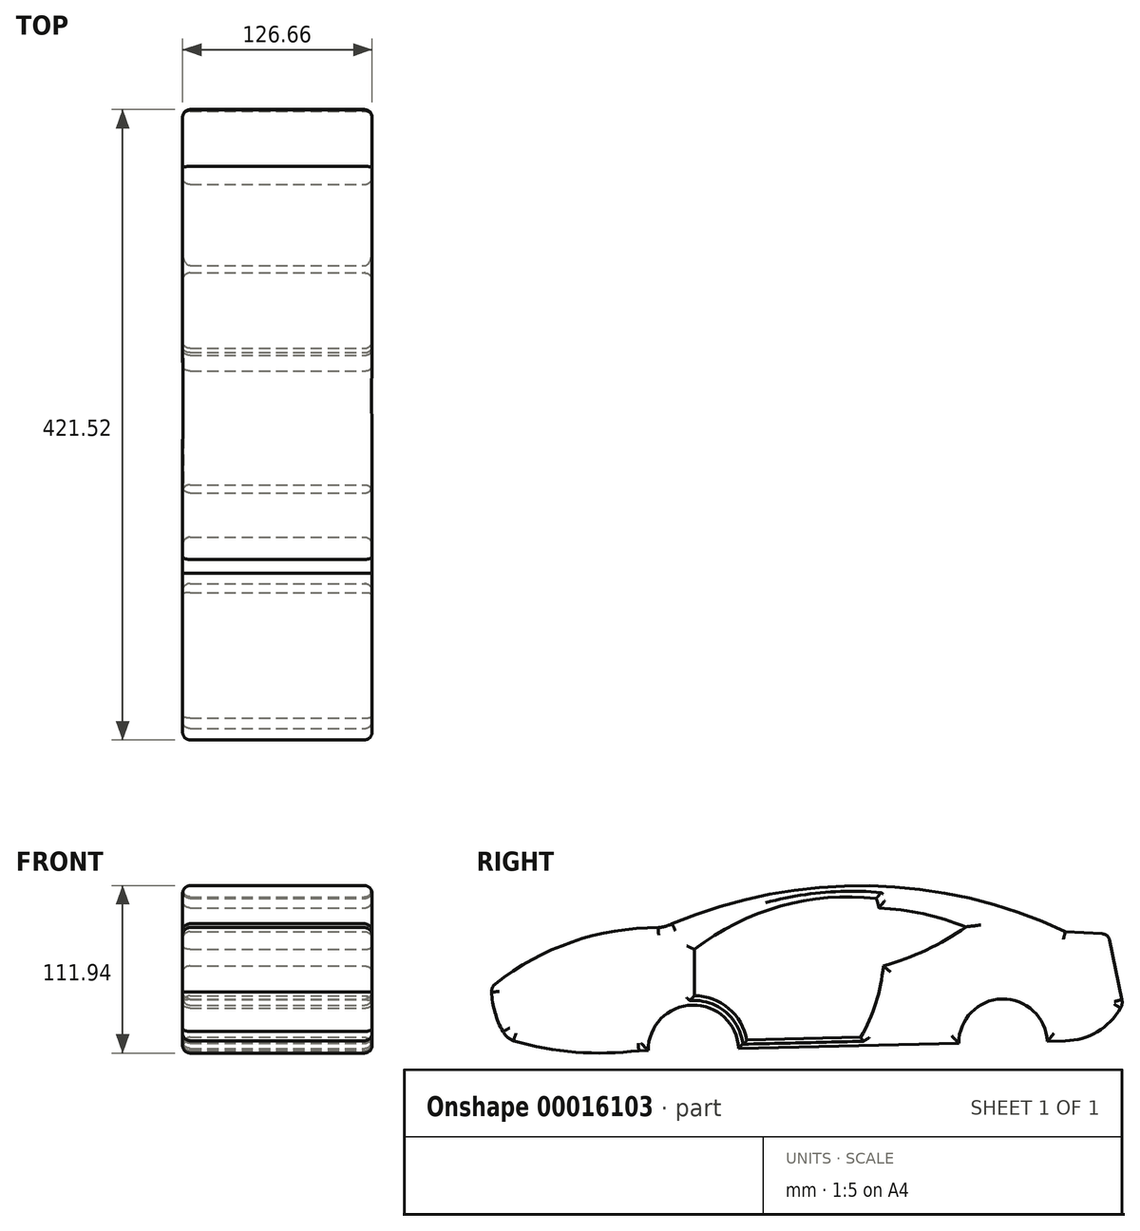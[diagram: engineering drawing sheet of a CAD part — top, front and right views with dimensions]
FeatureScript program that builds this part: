
annotation { "Feature Type Name" : "Feature", "Feature Type Description" : "" }
export const myFeature = defineFeature(function(context is Context, id is Id, definition is map)
    precondition{}
    {
        {
            var Q0;
            Q0=qCreatedBy(makeId("Right.planeOp"),FACE);
            var sketch = newSketch(context, id + "F0", { "sketchPlane" : qUnion([Q0])});
            skArc(sketch, "E0", {"start": v(-83.48, 39.7) * mm, "mid": v(-78.75, 40.5) * mm, "end": v(-74.28, 42.24) * mm});
            skArc(sketch, "E1", {"start": v(188.64, 37) * mm, "mid": v(57.74, 67.65) * mm, "end": v(-74.28, 42.24) * mm});
            skArc(sketch, "E2", {"start": v(-83.48, 39.7) * mm, "mid": v(-141.17, 30.08) * mm, "end": v(-192.5, 2.04) * mm});
            skArc(sketch, "E3", {"start": v(140.42, 60.51) * mm, "mid": v(137.05, 59.2) * mm, "end": v(134.3, 56.86) * mm});
            skArc(sketch, "E4", {"start": v(140.42, 60.51) * mm, "mid": v(129.16, 62.69) * mm, "end": v(117.85, 60.78) * mm});
            skLineSegment(sketch, "E5", {"start": v(188.64, 37) * mm, "end": v(217.28, 35.28) * mm});
            skArc(sketch, "E6", {"start": v(225.5, -14.08) * mm, "mid": v(226.53, -11.4) * mm, "end": v(226.34, -8.53) * mm});
            skLineSegment(sketch, "E7", {"start": v(226.34, -8.53) * mm, "end": v(217.28, 35.28) * mm});
            skArc(sketch, "E8", {"start": v(188.64, -36.07) * mm, "mid": v(209.97, -29.93) * mm, "end": v(225.5, -14.08) * mm});
            skArc(sketch, "E9", {"start": v(-29.85, -41.03) * mm, "mid": v(-60.8, -12.14) * mm, "end": v(-90.3, -42.51) * mm});
            skLineSegment(sketch, "E10", {"start": v(-90.3, -42.51) * mm, "end": v(-96.57, -42.66) * mm});
            skArc(sketch, "E11", {"start": v(176.48, -36.35) * mm, "mid": v(146.27, -8.07) * mm, "end": v(117.37, -37.69) * mm});
            skLineSegment(sketch, "E12", {"start": v(176.48, -36.35) * mm, "end": v(188.64, -36.07) * mm});
            skLineSegment(sketch, "E13", {"start": v(117.37, -37.69) * mm, "end": v(-29.85, -41.03) * mm});
            skPoint(sketch, "E14", {"position": v(-78.75, 40.5) * mm});
            skPoint(sketch, "E15.visualSharp", {"position": v(-195.03, 0) * mm});
            skArc(sketch, "E15.filletArc", {"start": v(-192.5, 2.04) * mm, "mid": v(-194.36, -0.36) * mm, "end": v(-194.9, -3.36) * mm});
            skArc(sketch, "E16", {"start": v(-187.3, -29.8) * mm, "mid": v(-184.44, -33.58) * mm, "end": v(-180.37, -36) * mm});
            skPoint(sketch, "E17", {"position": v(-180.37, -36) * mm});
            skPoint(sketch, "E18", {"position": v(-187.3, -29.8) * mm});
            skArc(sketch, "E19", {"start": v(-180.37, -36) * mm, "mid": v(-138.8, -43.56) * mm, "end": v(-96.57, -42.66) * mm});
            skArc(sketch, "E20", {"start": v(-194.9, -3.36) * mm, "mid": v(-192.72, -17.05) * mm, "end": v(-187.3, -29.8) * mm});
            skLineSegment(sketch, "E21", {"start": v(-59.36, 25.5) * mm, "end": v(-59.36, -5.92) * mm});
            skArc(sketch, "E22", {"start": v(-24.3, -35.53) * mm, "mid": v(-36.46, -14.36) * mm, "end": v(-59.36, -5.92) * mm});
            skArc(sketch, "E23", {"start": v(62.24, 59.21) * mm, "mid": v(-1.9, 54.03) * mm, "end": v(-59.36, 25.05) * mm});
            skArc(sketch, "E24", {"start": v(122.1, 40.18) * mm, "mid": v(93.57, 48.87) * mm, "end": v(64, 52.88) * mm});
            skArc(sketch, "E25", {"start": v(55.2, 53.43) * mm, "mid": v(-0.36, 46.83) * mm, "end": v(-51.63, 24.43) * mm});
            skArc(sketch, "E26", {"start": v(-51.71, 24.4) * mm, "mid": v(2.04, 10.5) * mm, "end": v(57.48, 13.55) * mm});
            skArc(sketch, "E27", {"start": v(66.94, 14.01) * mm, "mid": v(95.68, 24.66) * mm, "end": v(122.1, 40.18) * mm});
            skArc(sketch, "E28", {"start": v(57.48, 13.55) * mm, "mid": v(59.2, 33.8) * mm, "end": v(54.78, 53.62) * mm});
            skArc(sketch, "E29", {"start": v(51.86, -33.64) * mm, "mid": v(66.7, 11.7) * mm, "end": v(62.24, 59.21) * mm});
            skLineSegment(sketch, "E30", {"start": v(-24.3, -35.53) * mm, "end": v(51.86, -33.64) * mm});
            skPoint(sketch, "E31.rect.middle", {"position": v(122.82, 6.83) * mm});
            skSolve(sketch);
        }
        {
            var Q0;
            {var subQ1=sQuery(id+"F0.wireOp",EDGE,"E0");Q0=makeQuery(id+"F0.imprint","IMPRINT",FACE,{"disambiguationData":[TD([[makeQuery(id+"F0.imprint","IMPRINT",EDGE,{"derivedFrom":subQ1}),-1.0]])]});}
            extrude(context, id + "F1", {"entities" : qUnion([Q0]), "oppositeDirection" : true, "depth" : 126.66 * mm});
        }
        {
            var Q0;
            Q0=makeQuery(id+"F1.opExtrude","SWEPT_EDGE",EDGE,{"disambiguationData":[OSD([sQuery(id+"F0.wireOp",EDGE,"E5"),sQuery(id+"F0.wireOp",EDGE,"E7")])]});
            fillet(context, id + "F2", {"entities" : qUnion([Q0]), "radius" : 5.08 * mm, "tangentPropagation" : true, "allowEdgeOverflow" : false});
        }
        {
            var Q0;
            Q0=makeQuery(id+"F1.opExtrude","CAP_FACE",FACE,{"disambiguationData":[OSD([sQuery(id+"F0.wireOp",EDGE,"E0"),sQuery(id+"F0.wireOp",EDGE,"E1"),sQuery(id+"F0.wireOp",EDGE,"E2"),sQuery(id+"F0.wireOp",EDGE,"E5"),sQuery(id+"F0.wireOp",EDGE,"E6"),sQuery(id+"F0.wireOp",EDGE,"E7"),sQuery(id+"F0.wireOp",EDGE,"E8"),sQuery(id+"F0.wireOp",EDGE,"E9"),sQuery(id+"F0.wireOp",EDGE,"E10"),sQuery(id+"F0.wireOp",EDGE,"E11"),sQuery(id+"F0.wireOp",EDGE,"E12"),sQuery(id+"F0.wireOp",EDGE,"E13"),sQuery(id+"F0.wireOp",EDGE,"E15.filletArc"),sQuery(id+"F0.wireOp",EDGE,"E16"),sQuery(id+"F0.wireOp",EDGE,"E19"),sQuery(id+"F0.wireOp",EDGE,"E20"),sQuery(id+"F0.wireOp",EDGE,"E21"),sQuery(id+"F0.wireOp",EDGE,"E22"),sQuery(id+"F0.wireOp",EDGE,"E23"),sQuery(id+"F0.wireOp",EDGE,"E24"),sQuery(id+"F0.wireOp",EDGE,"E27"),sQuery(id+"F0.wireOp",EDGE,"E29"),sQuery(id+"F0.wireOp",EDGE,"E30")])],"isStart":true});
            fillet(context, id + "F3", {"entities" : qUnion([Q0]), "radius" : 5.08 * mm, "tangentPropagation" : true, "allowEdgeOverflow" : false});
        }
        {
            var Q0;
            Q0=makeQuery(id+"F1.opExtrude","CAP_FACE",FACE,{"disambiguationData":[OSD([sQuery(id+"F0.wireOp",EDGE,"E0"),sQuery(id+"F0.wireOp",EDGE,"E1"),sQuery(id+"F0.wireOp",EDGE,"E2"),sQuery(id+"F0.wireOp",EDGE,"E5"),sQuery(id+"F0.wireOp",EDGE,"E6"),sQuery(id+"F0.wireOp",EDGE,"E7"),sQuery(id+"F0.wireOp",EDGE,"E8"),sQuery(id+"F0.wireOp",EDGE,"E9"),sQuery(id+"F0.wireOp",EDGE,"E10"),sQuery(id+"F0.wireOp",EDGE,"E11"),sQuery(id+"F0.wireOp",EDGE,"E12"),sQuery(id+"F0.wireOp",EDGE,"E13"),sQuery(id+"F0.wireOp",EDGE,"E15.filletArc"),sQuery(id+"F0.wireOp",EDGE,"E16"),sQuery(id+"F0.wireOp",EDGE,"E19"),sQuery(id+"F0.wireOp",EDGE,"E20"),sQuery(id+"F0.wireOp",EDGE,"E21"),sQuery(id+"F0.wireOp",EDGE,"E22"),sQuery(id+"F0.wireOp",EDGE,"E23"),sQuery(id+"F0.wireOp",EDGE,"E24"),sQuery(id+"F0.wireOp",EDGE,"E27"),sQuery(id+"F0.wireOp",EDGE,"E29"),sQuery(id+"F0.wireOp",EDGE,"E30")])],"isStart":false});
            fillet(context, id + "F4", {"entities" : qUnion([Q0]), "radius" : 5.08 * mm, "tangentPropagation" : true, "allowEdgeOverflow" : false});
        }
    });
